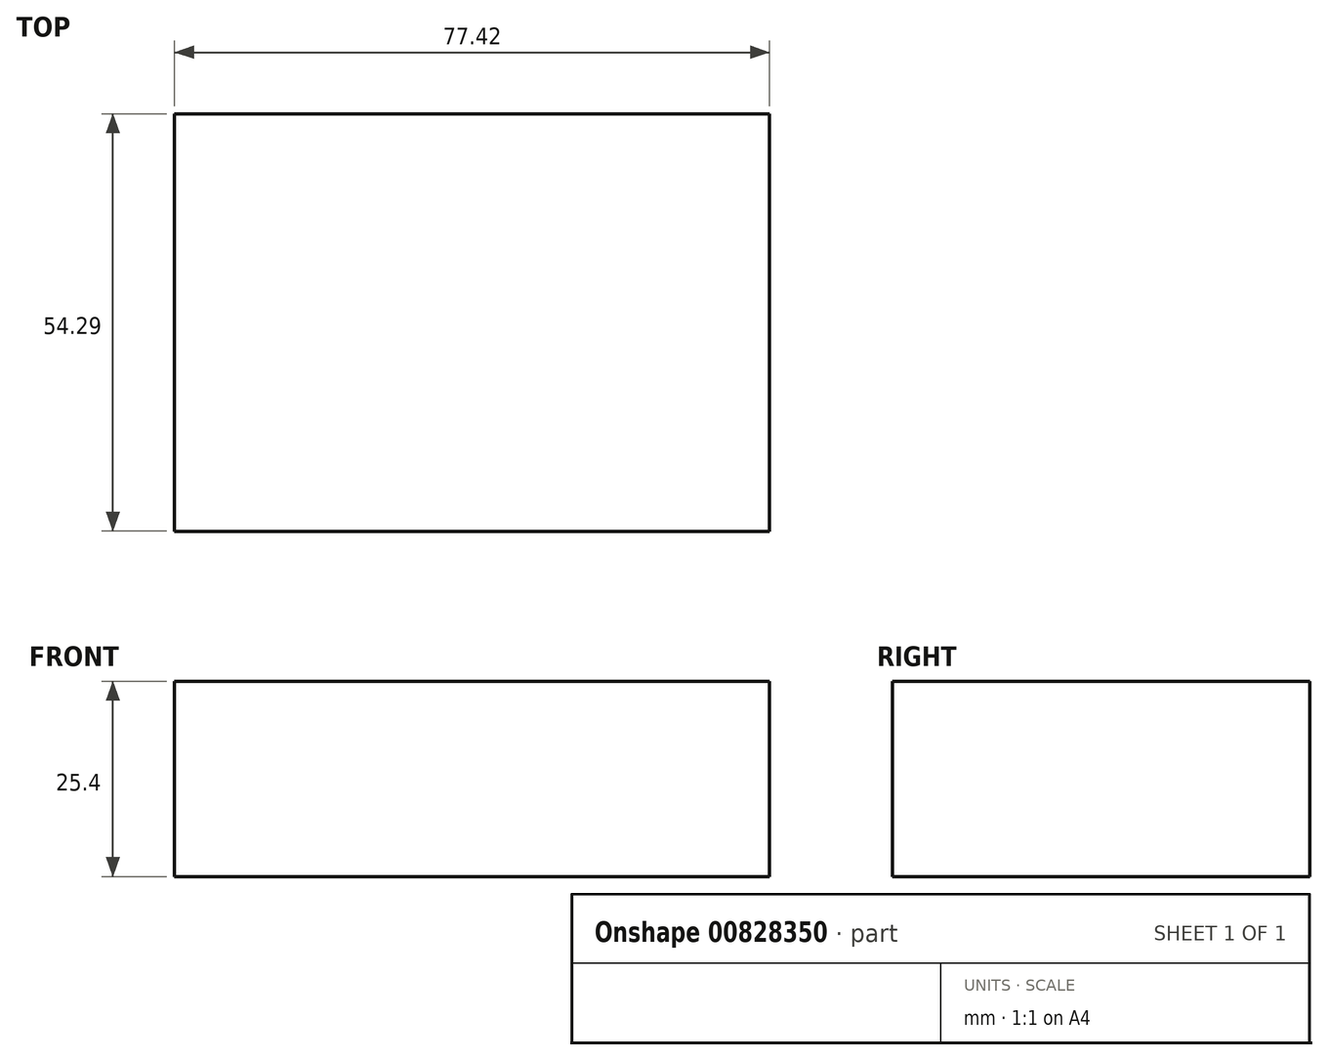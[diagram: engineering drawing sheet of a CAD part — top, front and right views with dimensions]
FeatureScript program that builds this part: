
annotation { "Feature Type Name" : "Feature", "Feature Type Description" : "" }
export const myFeature = defineFeature(function(context is Context, id is Id, definition is map)
    precondition{}
    {
        {
            var Q0;
            Q0=qCreatedBy(makeId("Top.planeOp"),FACE);
            var sketch = newSketch(context, id + "F0", { "sketchPlane" : qUnion([Q0])});
            skLineSegment(sketch, "E0.bottom", {"start": v(0, 0) * mm, "end": v(77.42, 0) * mm});
            skLineSegment(sketch, "E0.top", {"start": v(0, -54.3) * mm, "end": v(77.42, -54.3) * mm});
            skLineSegment(sketch, "E0.left", {"start": v(0, 0) * mm, "end": v(0, -54.3) * mm});
            skLineSegment(sketch, "E0.right", {"start": v(77.42, 0) * mm, "end": v(77.42, -54.3) * mm});
            skSolve(sketch);
        }
        {
            var Q0;
            Q0 = qSketchRegion(id + "F0", true);
            extrude(context, id + "F1", {"entities" : qUnion([Q0]), "depth" : 25.4 * mm, "offsetDistance" : 25.4 * mm});
        }
        {
            var Q0;
            Q0=makeQuery(id+"F1.opExtrude","CAP_FACE",FACE,{"disambiguationData":[OSD([sQuery(id+"F0.wireOp",EDGE,"E0.bottom"),sQuery(id+"F0.wireOp",EDGE,"E0.top"),sQuery(id+"F0.wireOp",EDGE,"E0.left"),sQuery(id+"F0.wireOp",EDGE,"E0.right")])],"isStart":false});
            var sketch = newSketch(context, id + "F2", { "sketchPlane" : qUnion([Q0])});
            skCircle(sketch, "E1", {"center": v(38.2, -26.75) * mm, "radius": 13.92 * mm});
            skSolve(sketch);
        }
        {
            var Q0;
            Q0=sQuery(id+"F2.wireOp",EDGE,"E1");
            extrude(context, id + "F3", {"bodyType" : ToolBodyType.SURFACE, "surfaceEntities" : qUnion([Q0]), "oppositeDirection" : true, "depth" : 25.4 * mm, "offsetDistance" : 25.4 * mm});
        }
    });
